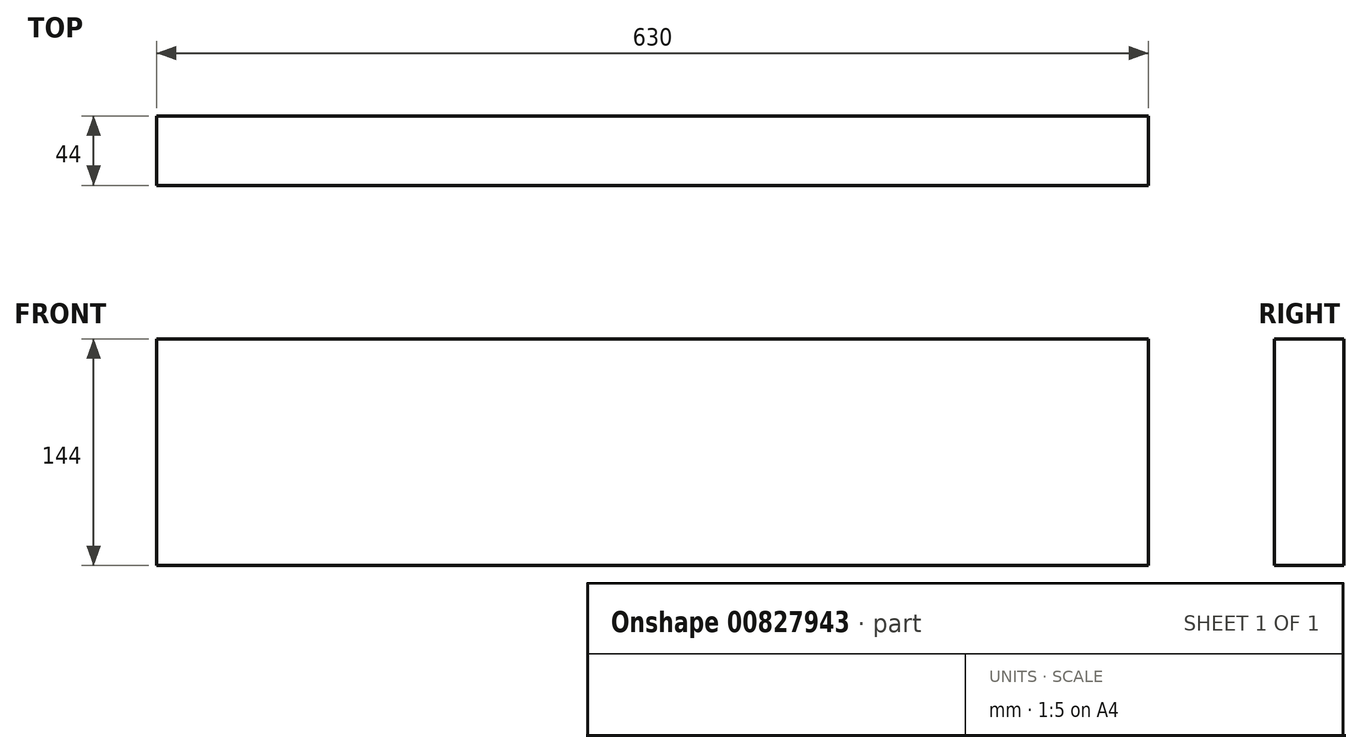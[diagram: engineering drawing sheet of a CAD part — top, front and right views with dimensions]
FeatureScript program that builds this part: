
annotation { "Feature Type Name" : "Feature", "Feature Type Description" : "" }
export const myFeature = defineFeature(function(context is Context, id is Id, definition is map)
    precondition{}
    {
        {
            var Q0;
            Q0=qCreatedBy(makeId("Top.planeOp"),FACE);
            var sketch = newSketch(context, id + "F0", { "sketchPlane" : qUnion([Q0])});
            skLineSegment(sketch, "E0.bottom", {"start": v(-315, 22) * mm, "end": v(315, 22) * mm});
            skLineSegment(sketch, "E0.top", {"start": v(-315, -22) * mm, "end": v(315, -22) * mm});
            skLineSegment(sketch, "E0.left", {"start": v(-315, 22) * mm, "end": v(-315, -22) * mm});
            skLineSegment(sketch, "E0.right", {"start": v(315, 22) * mm, "end": v(315, -22) * mm});
            skPoint(sketch, "E0.middle", {"position": v(0, 0) * mm});
            skSolve(sketch);
        }
        {
            var Q0;
            Q0=makeQuery(id+"F0.imprint","IMPRINT",FACE,{"disambiguationData":[TD([[makeQuery(id+"F0.imprint","IMPRINT",EDGE,{"derivedFrom":sQuery(id+"F0.wireOp",EDGE,"E0.bottom")}),-1.0]])]});
            extrude(context, id + "F1", {"entities" : qUnion([Q0]), "depth" : 144 * mm, "offsetDistance" : 25 * mm});
        }
    });
